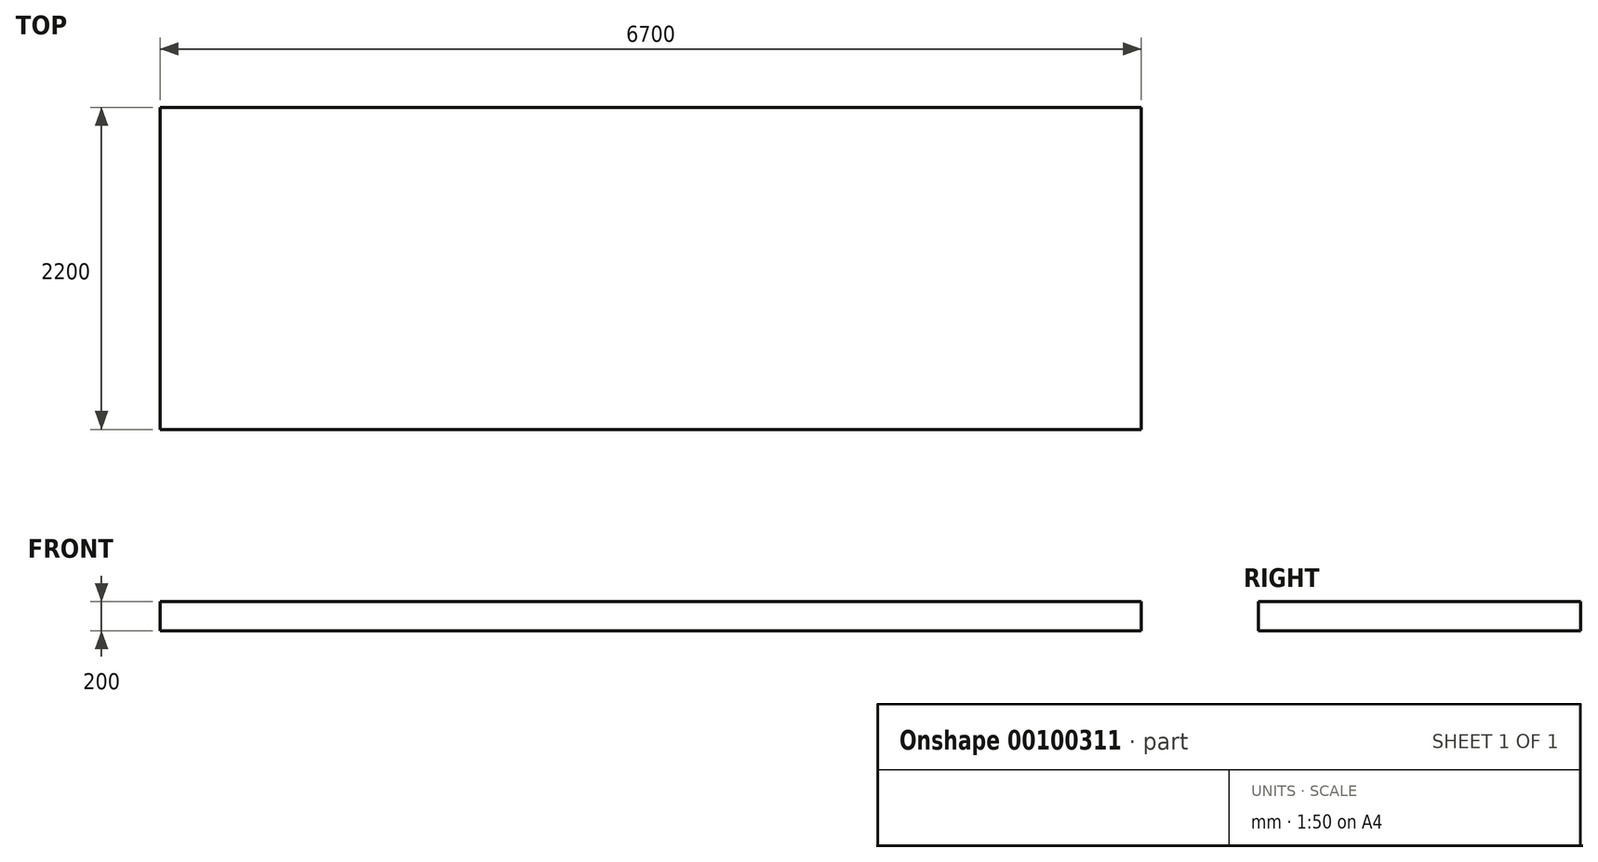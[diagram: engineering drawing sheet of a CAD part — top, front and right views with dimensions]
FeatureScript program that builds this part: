
annotation { "Feature Type Name" : "Feature", "Feature Type Description" : "" }
export const myFeature = defineFeature(function(context is Context, id is Id, definition is map)
    precondition{}
    {
        {
            var Q0;
            Q0=qCreatedBy(makeId("Top.planeOp"),FACE);
            var sketch = newSketch(context, id + "F0", { "sketchPlane" : qUnion([Q0])});
            skLineSegment(sketch, "E0.bottom", {"start": v(-3350.27, 808.45) * mm, "end": v(3349.73, 808.45) * mm});
            skLineSegment(sketch, "E0.top", {"start": v(-3350.27, -1391.55) * mm, "end": v(3349.73, -1391.55) * mm});
            skLineSegment(sketch, "E0.left", {"start": v(-3350.27, 808.45) * mm, "end": v(-3350.27, -1391.55) * mm});
            skLineSegment(sketch, "E0.right", {"start": v(3349.73, 808.45) * mm, "end": v(3349.73, -1391.55) * mm});
            skSolve(sketch);
        }
        {
            var Q0;
            Q0=makeQuery(id+"F0.imprint","IMPRINT",FACE,{"disambiguationData":[TD([[makeQuery(id+"F0.imprint","IMPRINT",EDGE,{"derivedFrom":sQuery(id+"F0.wireOp",EDGE,"E0.bottom")}),-1.0]])]});
            extrude(context, id + "F1", {"entities" : qUnion([Q0]), "depth" : 200 * mm});
        }
    });
